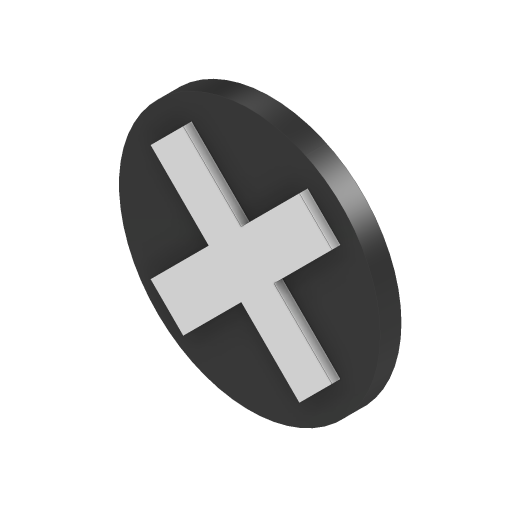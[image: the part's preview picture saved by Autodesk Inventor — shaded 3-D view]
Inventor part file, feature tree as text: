
AUTODESK INVENTOR PART (.ipt)
format: ipt  version: 2023 (Build 270158000, 158)  size: 262,656 bytes
history: native  units: mm
features: extrude x2, sketch x2, other x1
ambient origin geometry x8: Origin, YZ Plane, XZ Plane, XY Plane, X Axis, Y Axis, Z Axis, Center Point
bodies: Body1 (feature_tree)
feature tree (5):
  other  "Těleso1"
  extrude  "Vysunutí1"  Depth=12.4mm
  extrude  "Vysunutí2"  Depth=1.0mm TaperAngle=0.0deg
  sketch  "Náčrt1"
  sketch  "Náčrt2"
